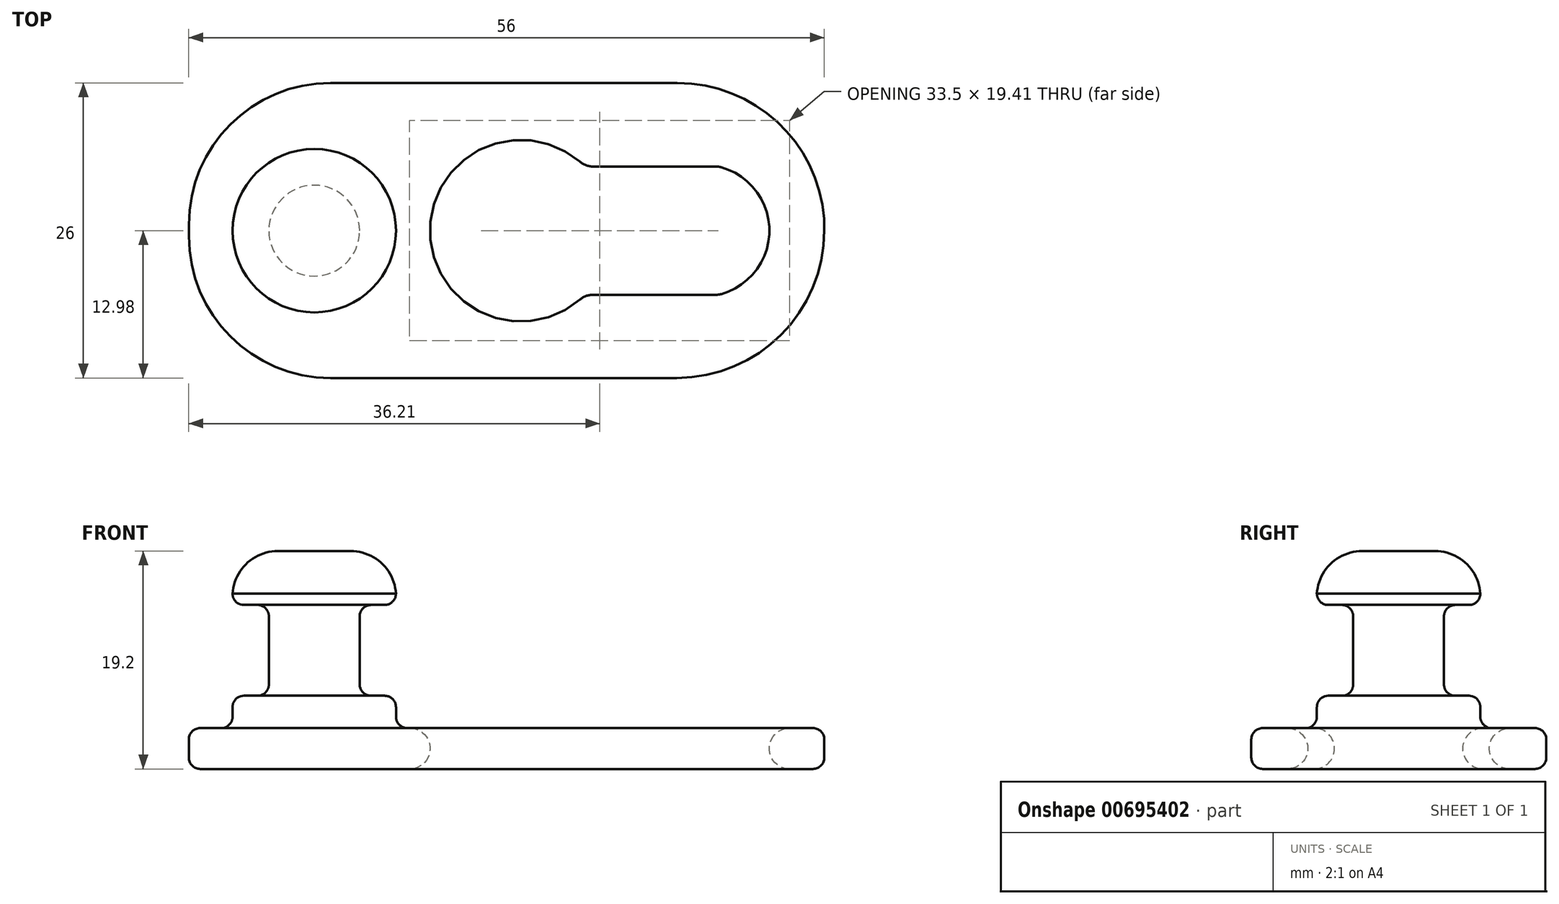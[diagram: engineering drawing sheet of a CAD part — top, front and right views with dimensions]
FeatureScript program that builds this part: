
annotation { "Feature Type Name" : "Feature", "Feature Type Description" : "" }
export const myFeature = defineFeature(function(context is Context, id is Id, definition is map)
    precondition{}
    {
        {
            var Q0;
            Q0=qCreatedBy(makeId("Top.planeOp"),FACE);
            var sketch = newSketch(context, id + "F0", { "sketchPlane" : qUnion([Q0])});
            skLineSegment(sketch, "E0", {"start": v(0, 52.84) * mm, "end": v(0, -52.67) * mm, "construction": true});
            skLineSegment(sketch, "E1", {"start": v(-57.06, 0) * mm, "end": v(21.4, 0) * mm, "construction": true});
            skLineSegment(sketch, "E2.0", {"start": v(-29.76, 0.52) * mm, "end": v(-29.76, 0) * mm});
            skLineSegment(sketch, "E3.0", {"start": v(-17.26, -12.98) * mm, "end": v(13.24, -12.98) * mm});
            skLineSegment(sketch, "E4.0", {"start": v(-17.26, 13.02) * mm, "end": v(13.28, 13.02) * mm});
            skArc(sketch, "E5", {"start": v(5.16, 5.65) * mm, "mid": v(-8.5, 0) * mm, "end": v(5.16, -5.65) * mm});
            skArc(sketch, "E6", {"start": v(16.91, -5.65) * mm, "mid": v(21.4, 0) * mm, "end": v(16.91, 5.65) * mm});
            skLineSegment(sketch, "E7", {"start": v(16.91, 5.65) * mm, "end": v(5.16, 5.65) * mm});
            skLineSegment(sketch, "E8", {"start": v(16.91, -5.65) * mm, "end": v(5.16, -5.65) * mm});
            skPoint(sketch, "E9.0.start.orphan", {"position": v(16.05, 13) * mm});
            skPoint(sketch, "E10.trimOffspring.end.orphan", {"position": v(16.05, -13) * mm});
            skCircle(sketch, "E11", {"center": v(-18.76, 0) * mm, "radius": 7.2 * mm});
            skLineSegment(sketch, "E12", {"start": v(-11.56, 0) * mm, "end": v(-11.56, -14.31) * mm, "construction": true});
            skLineSegment(sketch, "E13", {"start": v(-25.96, 0) * mm, "end": v(-25.96, -14.7) * mm, "construction": true});
            skLineSegment(sketch, "E14", {"start": v(21.4, 0) * mm, "end": v(46.22, 0) * mm, "construction": true});
            skLineSegment(sketch, "E15", {"start": v(-8.5, 0) * mm, "end": v(-8.5, -14.52) * mm, "construction": true});
            skPoint(sketch, "E16.visualSharp", {"position": v(-29.06, 13) * mm});
            skArc(sketch, "E16.filletArc", {"start": v(-17.26, 13.02) * mm, "mid": v(-26.1, 9.36) * mm, "end": v(-29.76, 0.52) * mm});
            skArc(sketch, "E17.filletArc", {"start": v(-29.76, -0.48) * mm, "mid": v(-26.1, -9.32) * mm, "end": v(-17.26, -12.98) * mm});
            skPoint(sketch, "E18.visualSharp", {"position": v(26.94, 13) * mm});
            skArc(sketch, "E18.filletArc", {"start": v(26.24, 1.03) * mm, "mid": v(22.11, 9.56) * mm, "end": v(13.28, 13.02) * mm});
            skArc(sketch, "E19.filletArc", {"start": v(13.24, -12.98) * mm, "mid": v(22.44, -9.17) * mm, "end": v(26.24, 0.02) * mm});
            skLineSegment(sketch, "E20", {"start": v(-29.76, 0) * mm, "end": v(-29.76, -0.48) * mm});
            skLineSegment(sketch, "E21", {"start": v(26.24, 1.03) * mm, "end": v(26.24, 0.02) * mm});
            skSolve(sketch);
        }
        {
            var Q0;
            Q0=makeQuery(id+"F0.imprint","IMPRINT",FACE,{"disambiguationData":[TD([[makeQuery(id+"F0.imprint","IMPRINT",EDGE,{"derivedFrom":sQuery(id+"F0.wireOp",EDGE,"E2.0")}),1.0]])]});
            var Q1;
            Q1=makeQuery(id+"F0.imprint","IMPRINT",FACE,{"disambiguationData":[TD([[makeQuery(id+"F0.imprint","IMPRINT",EDGE,{"derivedFrom":sQuery(id+"F0.wireOp",EDGE,"E11")}),1.0]])]});
            extrude(context, id + "F1", {"entities" : qUnion([Q0, Q1]), "depth" : 3.6 * mm, "offsetDistance" : 25 * mm});
        }
        {
            var Q0;
            Q0=makeQuery(id+"F1.opExtrude","SWEPT_FACE",FACE,{"disambiguationData":[OSD([sQuery(id+"F0.wireOp",EDGE,"E5")])]});
            var Q1;
            Q1=makeQuery(id+"F1.opExtrude","SWEPT_FACE",FACE,{"disambiguationData":[OSD([sQuery(id+"F0.wireOp",EDGE,"E7")])]});
            var Q2;
            Q2=makeQuery(id+"F1.opExtrude","SWEPT_FACE",FACE,{"disambiguationData":[OSD([sQuery(id+"F0.wireOp",EDGE,"E6")])]});
            var Q3;
            Q3=makeQuery(id+"F1.opExtrude","SWEPT_FACE",FACE,{"disambiguationData":[OSD([sQuery(id+"F0.wireOp",EDGE,"E8")])]});
            fillet(context, id + "F2", {"entities" : qUnion([Q0, Q1, Q2, Q3]), "radius" : 1.8 * mm, "tangentPropagation" : true, "allowEdgeOverflow" : false});
        }
        {
            var Q0;
            Q0=qCreatedBy(makeId("Top.planeOp"),FACE);
            var sketch = newSketch(context, id + "F3", { "sketchPlane" : qUnion([Q0])});
            skCircle(sketch, "E22", {"center": v(-18.7, 0) * mm, "radius": 7.2 * mm});
            skSolve(sketch);
        }
        {
            var Q0;
            Q0=qSketchRegion(id+"F3",true);
            extrude(context, id + "F4", {"entities" : qUnion([Q0]), "operationType" : NewBodyOperationType.ADD, "depth" : 6.45 * mm, "offsetDistance" : 25 * mm});
        }
        {
            var Q0;
            Q0=makeQuery(id+"F4.opExtrude","CAP_FACE",FACE,{"disambiguationData":[OSD([sQuery(id+"F3.wireOp",EDGE,"E22")])],"isStart":false});
            var sketch = newSketch(context, id + "F5", { "sketchPlane" : qUnion([Q0])});
            skCircle(sketch, "E23", {"center": v(-18.7, 0) * mm, "radius": 4 * mm});
            skSolve(sketch);
        }
        {
            var Q0;
            Q0=makeQuery(id+"F5.imprint","IMPRINT",FACE,{"disambiguationData":[TD([[makeQuery(id+"F5.imprint","IMPRINT",EDGE,{"derivedFrom":sQuery(id+"F5.wireOp",EDGE,"E23")}),1.0]])]});
            extrude(context, id + "F6", {"entities" : qUnion([Q0]), "operationType" : NewBodyOperationType.ADD, "depth" : 8 * mm, "offsetDistance" : 25 * mm});
        }
        {
            var Q0;
            Q0=makeQuery(id+"F6.opExtrude","CAP_FACE",FACE,{"disambiguationData":[OSD([sQuery(id+"F5.wireOp",EDGE,"E23")])],"isStart":false});
            var sketch = newSketch(context, id + "F7", { "sketchPlane" : qUnion([Q0])});
            skCircle(sketch, "E24", {"center": v(-18.7, 0) * mm, "radius": 7.2 * mm});
            skSolve(sketch);
        }
        {
            var Q0;
            Q0=makeQuery(id+"F4.opExtrude","CAP_FACE",FACE,{"disambiguationData":[OSD([sQuery(id+"F3.wireOp",EDGE,"E22")])],"isStart":false});
            var Q1;
            Q1=makeQuery(id+"F4.opExtrude","SWEPT_FACE",FACE,{"disambiguationData":[OSD([sQuery(id+"F3.wireOp",EDGE,"E22")])]});
            fillet(context, id + "F8", {"entities" : qUnion([Q0, Q1]), "radius" : 1 * mm, "allowEdgeOverflow" : false});
        }
        {
            var Q0;
            Q0=makeQuery(id+"F7.imprint","IMPRINT",FACE,{"disambiguationData":[TD([[makeQuery(id+"F7.imprint","IMPRINT",EDGE,{"derivedFrom":sQuery(id+"F7.wireOp",EDGE,"E24")}),1.0]])]});
            var Q1;
            Q1=makeQuery(id+"F7.imprint","IMPRINT",FACE,{"disambiguationData":[TD([[makeQuery(id+"F7.imprint","IMPRINT",EDGE,{"derivedFrom":makeQuery(id+"F6.opExtrude","CAP_EDGE",EDGE,{"disambiguationData":[OSD([sQuery(id+"F5.wireOp",EDGE,"E23")])],"isStart":false})}),1.0]])]});
            extrude(context, id + "F9", {"entities" : qUnion([Q0, Q1]), "operationType" : NewBodyOperationType.ADD, "depth" : 4.75 * mm, "offsetDistance" : 25 * mm});
        }
        {
            var Q0;
            Q0=makeQuery(id+"F9.opExtrude","CAP_FACE",FACE,{"disambiguationData":[OSD([sQuery(id+"F7.wireOp",EDGE,"E24")])],"isStart":true});
            var Q1;
            Q1=makeQuery(id+"F6.opExtrude","SWEPT_FACE",FACE,{"disambiguationData":[OSD([sQuery(id+"F5.wireOp",EDGE,"E23")])]});
            fillet(context, id + "F10", {"entities" : qUnion([Q0, Q1]), "radius" : 1 * mm, "tangentPropagation" : true, "allowEdgeOverflow" : false});
        }
        {
            var Q0;
            Q0=makeQuery(id+"F9.opExtrude","CAP_FACE",FACE,{"disambiguationData":[OSD([sQuery(id+"F7.wireOp",EDGE,"E24")])],"isStart":false});
            var Q1;
            Q1=makeQuery(id+"F9.opExtrude","SWEPT_FACE",FACE,{"disambiguationData":[OSD([sQuery(id+"F7.wireOp",EDGE,"E24")])]});
            fillet(context, id + "F11", {"entities" : qUnion([Q0, Q1]), "radius" : 4 * mm, "tangentPropagation" : true, "allowEdgeOverflow" : false});
        }
        {
            var Q0;
            Q0=makeQuery(id+"F1.opExtrude","CAP_FACE",FACE,{"disambiguationData":[OSD([sQuery(id+"F0.wireOp",EDGE,"E2.0"),sQuery(id+"F0.wireOp",EDGE,"E3.0"),sQuery(id+"F0.wireOp",EDGE,"E4.0"),sQuery(id+"F0.wireOp",EDGE,"E5"),sQuery(id+"F0.wireOp",EDGE,"E6"),sQuery(id+"F0.wireOp",EDGE,"E7"),sQuery(id+"F0.wireOp",EDGE,"E8"),sQuery(id+"F0.wireOp",EDGE,"E16.filletArc"),sQuery(id+"F0.wireOp",EDGE,"E17.filletArc"),sQuery(id+"F0.wireOp",EDGE,"E18.filletArc"),sQuery(id+"F0.wireOp",EDGE,"E19.filletArc"),sQuery(id+"F0.wireOp",EDGE,"E20")])],"isStart":false});
            var Q1;
            Q1=makeQuery(id+"F1.opExtrude","SWEPT_FACE",FACE,{"disambiguationData":[OSD([sQuery(id+"F0.wireOp",EDGE,"E17.filletArc")])]});
            var Q2;
            Q2=makeQuery(id+"F1.opExtrude","SWEPT_FACE",FACE,{"disambiguationData":[OSD([sQuery(id+"F0.wireOp",EDGE,"E3.0")])]});
            var Q3;
            Q3=makeQuery(id+"F1.opExtrude","SWEPT_FACE",FACE,{"disambiguationData":[OSD([sQuery(id+"F0.wireOp",EDGE,"E18.filletArc"),sQuery(id+"F0.wireOp",EDGE,"E19.filletArc")])]});
            var Q4;
            Q4=makeQuery(id+"F1.opExtrude","SWEPT_FACE",FACE,{"disambiguationData":[OSD([sQuery(id+"F0.wireOp",EDGE,"E4.0")])]});
            var Q5;
            Q5=makeQuery(id+"F1.opExtrude","SWEPT_FACE",FACE,{"disambiguationData":[OSD([sQuery(id+"F0.wireOp",EDGE,"E16.filletArc")])]});
            fillet(context, id + "F12", {"entities" : qUnion([Q0, Q1, Q2, Q3, Q4, Q5]), "radius" : 1 * mm, "tangentPropagation" : true, "allowEdgeOverflow" : false});
        }
    });
